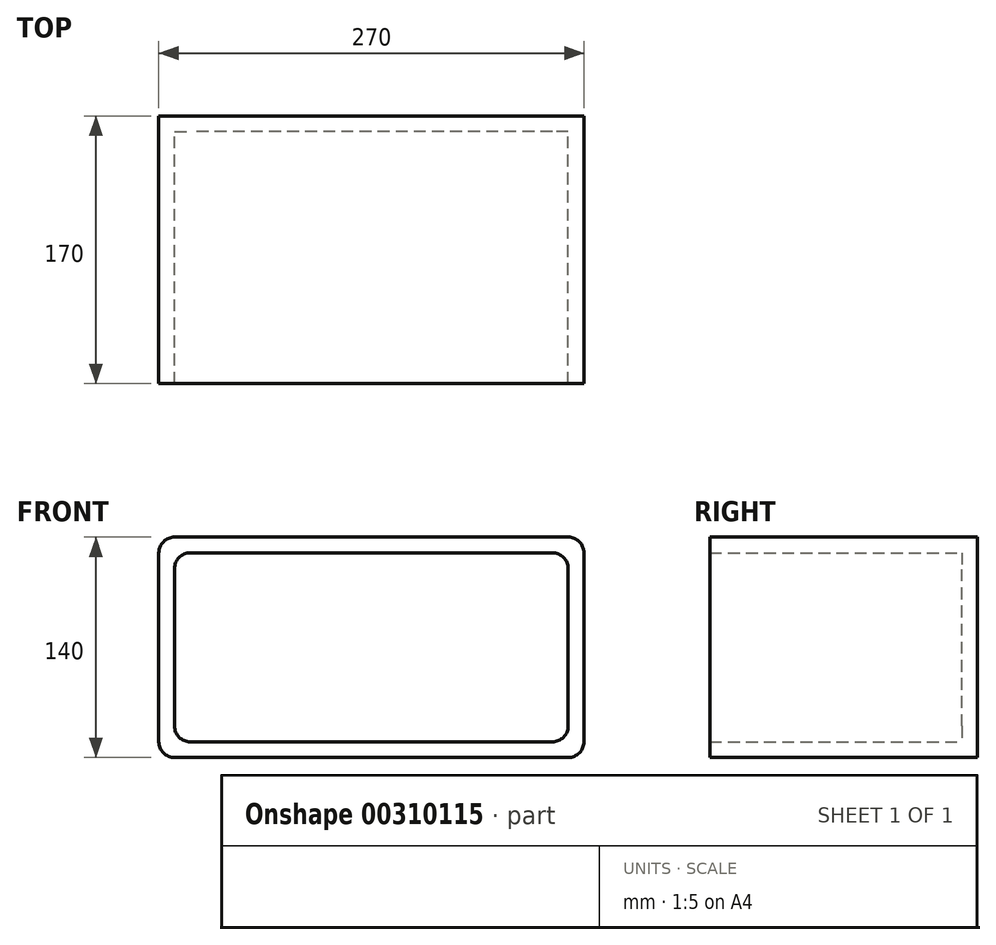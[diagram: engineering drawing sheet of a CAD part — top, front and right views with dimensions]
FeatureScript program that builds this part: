
annotation { "Feature Type Name" : "Feature", "Feature Type Description" : "" }
export const myFeature = defineFeature(function(context is Context, id is Id, definition is map)
    precondition{}
    {
        {
            var Q0;
            Q0=qCreatedBy(makeId("Front.planeOp"),FACE);
            var sketch = newSketch(context, id + "F0", { "sketchPlane" : qUnion([Q0])});
            skLineSegment(sketch, "E0.bottom", {"start": v(-125, 70) * mm, "end": v(125, 70) * mm});
            skLineSegment(sketch, "E0.top", {"start": v(-125, -70) * mm, "end": v(125, -70) * mm});
            skLineSegment(sketch, "E0.left", {"start": v(-135, 60) * mm, "end": v(-135, -60) * mm});
            skLineSegment(sketch, "E0.right", {"start": v(135, 60) * mm, "end": v(135, -60) * mm});
            skPoint(sketch, "E0.middle", {"position": v(0, 0) * mm});
            skPoint(sketch, "E1.visualSharp", {"position": v(135, 70) * mm});
            skArc(sketch, "E1.filletArc", {"start": v(135, 60) * mm, "mid": v(132.07, 67.07) * mm, "end": v(125, 70) * mm});
            skPoint(sketch, "E2.visualSharp", {"position": v(135, -70) * mm});
            skArc(sketch, "E2.filletArc", {"start": v(125, -70) * mm, "mid": v(132.07, -67.07) * mm, "end": v(135, -60) * mm});
            skPoint(sketch, "E3.visualSharp", {"position": v(-135, 70) * mm});
            skArc(sketch, "E3.filletArc", {"start": v(-125, 70) * mm, "mid": v(-132.07, 67.07) * mm, "end": v(-135, 60) * mm});
            skPoint(sketch, "E4.visualSharp", {"position": v(-135, -70) * mm});
            skArc(sketch, "E4.filletArc", {"start": v(-135, -60) * mm, "mid": v(-132.07, -67.07) * mm, "end": v(-125, -70) * mm});
            skLineSegment(sketch, "E5", {"start": v(-135, 70) * mm, "end": v(-125, 60) * mm});
            skLineSegment(sketch, "E6", {"start": v(-125, -50) * mm, "end": v(-125, 50) * mm});
            skLineSegment(sketch, "E7", {"start": v(-115, -60) * mm, "end": v(115, -60) * mm});
            skLineSegment(sketch, "E8", {"start": v(125, -50) * mm, "end": v(125, 50) * mm});
            skLineSegment(sketch, "E9", {"start": v(115, 60) * mm, "end": v(-115, 60) * mm});
            skArc(sketch, "E10.filletArc", {"start": v(-115, 60) * mm, "mid": v(-122.07, 57.07) * mm, "end": v(-125, 50) * mm});
            skPoint(sketch, "E11.newPointB", {"position": v(-125, -62.86) * mm});
            skArc(sketch, "E11.filletArc", {"start": v(-125, -50) * mm, "mid": v(-122.07, -57.07) * mm, "end": v(-115, -60) * mm});
            skArc(sketch, "E12.filletArc", {"start": v(115, -60) * mm, "mid": v(122.07, -57.07) * mm, "end": v(125, -50) * mm});
            skArc(sketch, "E13.filletArc", {"start": v(125, 50) * mm, "mid": v(122.07, 57.07) * mm, "end": v(115, 60) * mm});
            skSolve(sketch);
        }
        {
            var Q0;
            Q0 = qSketchRegion(id + "F0", true);
            extrude(context, id + "F1", {"entities" : qUnion([Q0]), "depth" : 160 * mm});
        }
        {
            var Q0;
            Q0=makeQuery(id+"F1.opExtrude","CAP_FACE",FACE,{"disambiguationData":[OSD([sQuery(id+"F0.wireOp",EDGE,"E0.bottom"),sQuery(id+"F0.wireOp",EDGE,"E0.top"),sQuery(id+"F0.wireOp",EDGE,"E0.left"),sQuery(id+"F0.wireOp",EDGE,"E0.right"),sQuery(id+"F0.wireOp",EDGE,"E1.filletArc"),sQuery(id+"F0.wireOp",EDGE,"E2.filletArc"),sQuery(id+"F0.wireOp",EDGE,"E3.filletArc"),sQuery(id+"F0.wireOp",EDGE,"E4.filletArc"),sQuery(id+"F0.wireOp",EDGE,"E6"),sQuery(id+"F0.wireOp",EDGE,"E7"),sQuery(id+"F0.wireOp",EDGE,"E8"),sQuery(id+"F0.wireOp",EDGE,"E9"),sQuery(id+"F0.wireOp",EDGE,"E10.filletArc"),sQuery(id+"F0.wireOp",EDGE,"E11.filletArc"),sQuery(id+"F0.wireOp",EDGE,"E12.filletArc"),sQuery(id+"F0.wireOp",EDGE,"E13.filletArc")])],"isStart":true});
            var sketch = newSketch(context, id + "F2", { "sketchPlane" : qUnion([Q0])});
            skLineSegment(sketch, "E14.bottom", {"start": v(-125, 70) * mm, "end": v(125, 70) * mm});
            skLineSegment(sketch, "E14.top", {"start": v(-125, -70) * mm, "end": v(125, -70) * mm});
            skLineSegment(sketch, "E14.left", {"start": v(-135, 60) * mm, "end": v(-135, -60) * mm});
            skLineSegment(sketch, "E14.right", {"start": v(135, 60) * mm, "end": v(135, -60) * mm});
            skPoint(sketch, "E14.middle", {"position": v(0, 0) * mm});
            skPoint(sketch, "E15.visualSharp", {"position": v(-135, 70) * mm});
            skArc(sketch, "E15.filletArc", {"start": v(-125, 70) * mm, "mid": v(-132.07, 67.07) * mm, "end": v(-135, 60) * mm});
            skPoint(sketch, "E16.visualSharp", {"position": v(-135, -70) * mm});
            skArc(sketch, "E16.filletArc", {"start": v(-135, -60) * mm, "mid": v(-132.07, -67.07) * mm, "end": v(-125, -70) * mm});
            skPoint(sketch, "E17.visualSharp", {"position": v(135, -70) * mm});
            skArc(sketch, "E17.filletArc", {"start": v(125, -70) * mm, "mid": v(132.07, -67.07) * mm, "end": v(135, -60) * mm});
            skPoint(sketch, "E18.visualSharp", {"position": v(135, 70) * mm});
            skArc(sketch, "E18.filletArc", {"start": v(135, 60) * mm, "mid": v(132.07, 67.07) * mm, "end": v(125, 70) * mm});
            skSolve(sketch);
        }
        {
            var Q0;
            Q0 = qSketchRegion(id + "F2", true);
            extrude(context, id + "F3", {"entities" : qUnion([Q0]), "operationType" : NewBodyOperationType.ADD, "depth" : 10 * mm});
        }
    });
